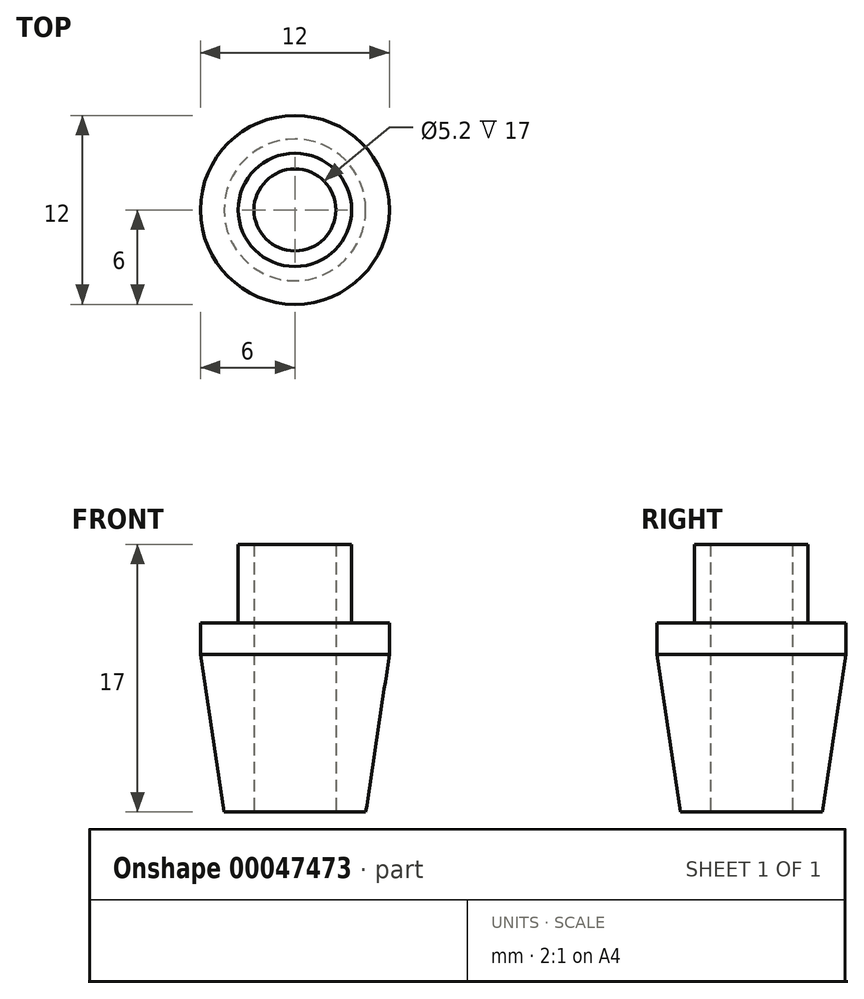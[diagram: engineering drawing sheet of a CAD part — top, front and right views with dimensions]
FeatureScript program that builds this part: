
annotation { "Feature Type Name" : "Feature", "Feature Type Description" : "" }
export const myFeature = defineFeature(function(context is Context, id is Id, definition is map)
    precondition{}
    {
        {
            var Q0;
            Q0=qCreatedBy(makeId("Top.planeOp"),FACE);
            var sketch = newSketch(context, id + "F0", { "sketchPlane" : qUnion([Q0])});
            skCircle(sketch, "E0", {"center": v(0, 0) * mm, "radius": 2.5 * mm, "construction": true});
            skCircle(sketch, "E1.0", {"center": v(0, 0) * mm, "radius": 4.5 * mm});
            skSolve(sketch);
        }
        {
            var Q0;
            Q0=qCreatedBy(makeId("Top.planeOp"),FACE);
            cPlane(context, id + "F1", {"entities" : qUnion([Q0]), "cplaneType" : CPlaneType.OFFSET, "offset" : 10 * mm, "width" : 150 * mm, "height" : 150 * mm});
        }
        {
            var Q0;
            Q0=qCreatedBy(id+"F1.planeOp",FACE);
            var sketch = newSketch(context, id + "F2", { "sketchPlane" : qUnion([Q0])});
            skCircle(sketch, "E2", {"center": v(0, 0) * mm, "radius": 6 * mm});
            skSolve(sketch);
        }
        {
            var Q0;
            Q0=makeQuery(id+"F0.imprint","IMPRINT",FACE,{"disambiguationData":[TD([[makeQuery(id+"F0.imprint","IMPRINT",EDGE,{"derivedFrom":sQuery(id+"F0.wireOp",EDGE,"E1.0")}),1.0]])]});
            var Q1;
            Q1=makeQuery(id+"F2.imprint","IMPRINT",FACE,{"disambiguationData":[TD([[makeQuery(id+"F2.imprint","IMPRINT",EDGE,{"derivedFrom":sQuery(id+"F2.wireOp",EDGE,"E2")}),1.0]])]});
            loft(context, id + "F3", {"sheetProfilesArray" : [{ "sheetProfileEntities" : qUnion([Q0]) }, { "sheetProfileEntities" : qUnion([Q1]) }]});
        }
        {
            var Q0;
            Q0=makeQuery(id+"F3.opLoft","CAP_FACE",FACE,{"disambiguationData":[OSD([makeQuery(id+"F2.imprint","IMPRINT",FACE,{"disambiguationData":[TD([[makeQuery(id+"F2.imprint","IMPRINT",EDGE,{"derivedFrom":sQuery(id+"F2.wireOp",EDGE,"E2")}),1.0]])]})])],"isStart":true});
            extrude(context, id + "F4", {"entities" : qUnion([Q0]), "operationType" : NewBodyOperationType.ADD, "depth" : 2 * mm});
        }
        {
            var Q0;
            Q0=makeQuery(id+"F4.opExtrude","CAP_FACE",FACE,{"disambiguationData":[OSD([makeQuery(id+"F2.imprint","IMPRINT",FACE,{"disambiguationData":[TD([[makeQuery(id+"F2.imprint","IMPRINT",EDGE,{"derivedFrom":sQuery(id+"F2.wireOp",EDGE,"E2")}),1.0]])]})])],"isStart":false});
            var sketch = newSketch(context, id + "F5", { "sketchPlane" : qUnion([Q0])});
            skCircle(sketch, "E3", {"center": v(0, 0) * mm, "radius": 3.6 * mm});
            skSolve(sketch);
        }
        {
            var Q0;
            Q0 = qSketchRegion(id + "F5", true);
            extrude(context, id + "F6", {"entities" : qUnion([Q0]), "operationType" : NewBodyOperationType.ADD, "depth" : 5 * mm});
        }
        {
            var Q0;
            Q0=sQuery(id+"F0.wireOp",VERTEX,"E0.center");
            var Q1;
            Q1=makeQuery(id+"F3.opLoft","SWEPT_BODY",BODY,{"disambiguationData":[OSD([makeQuery(id+"F0.imprint","IMPRINT",FACE,{"disambiguationData":[TD([[makeQuery(id+"F0.imprint","IMPRINT",EDGE,{"derivedFrom":sQuery(id+"F0.wireOp",EDGE,"E1.0")}),1.0]])]}),makeQuery(id+"F2.imprint","IMPRINT",FACE,{"disambiguationData":[TD([[makeQuery(id+"F2.imprint","IMPRINT",EDGE,{"derivedFrom":sQuery(id+"F2.wireOp",EDGE,"E2")}),1.0]])]})])]});
            hole(context, id + "F7", {"style" : HoleStyle.SIMPLE, "holeDiameter" : 5.2 * mm, "endStyle" : HoleEndStyle.THROUGH, "oppositeDirection" : true, "locations" : qUnion([Q0]), "scope" : qUnion([Q1])});
        }
    });
